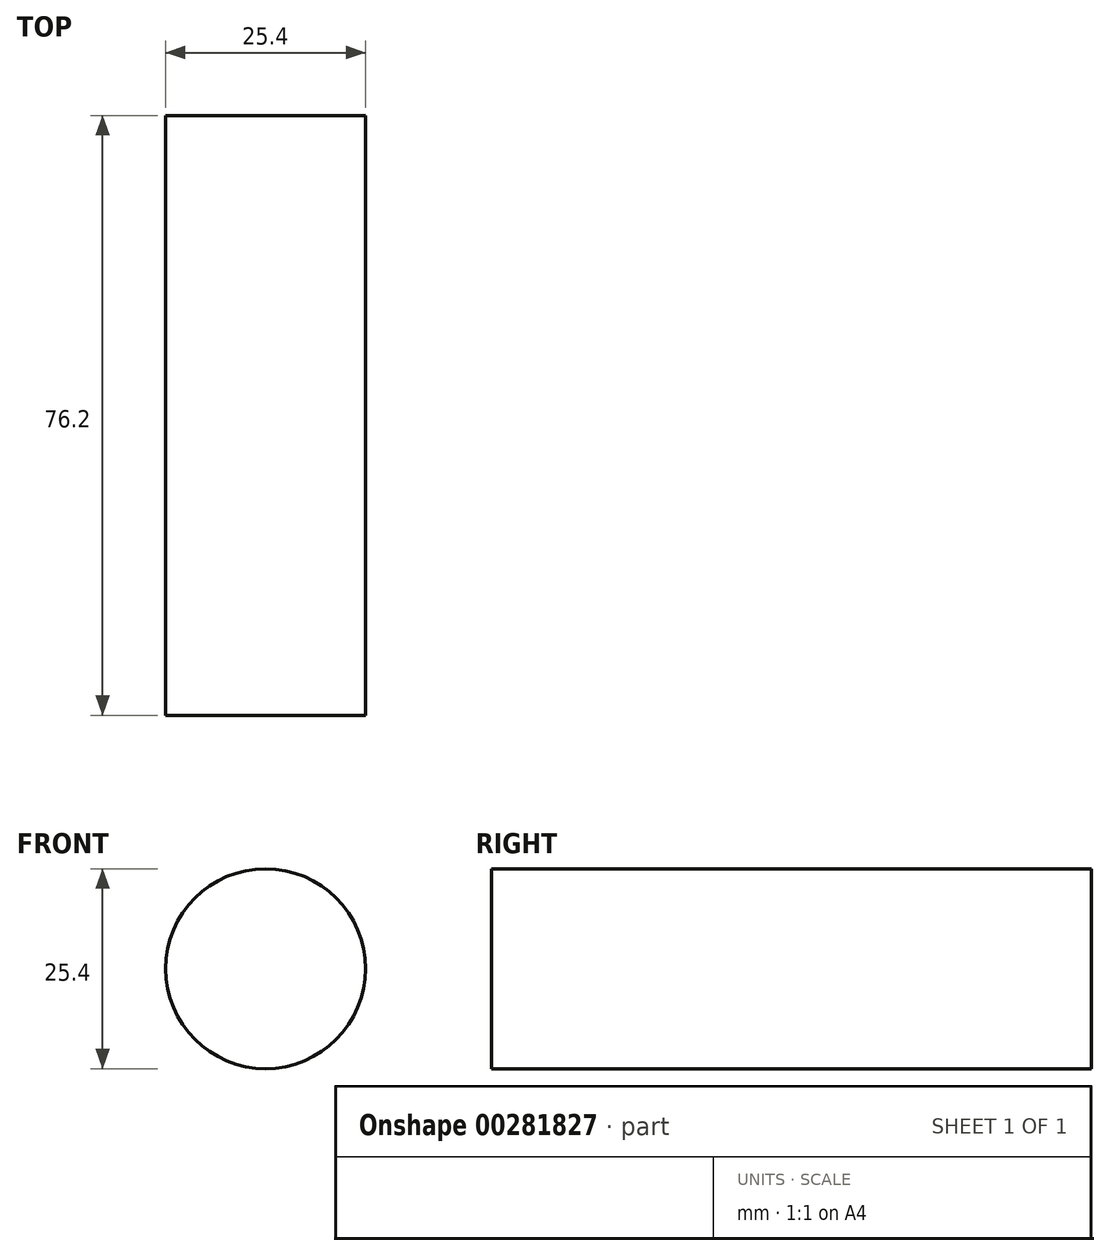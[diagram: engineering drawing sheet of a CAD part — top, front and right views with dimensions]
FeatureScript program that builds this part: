
annotation { "Feature Type Name" : "Feature", "Feature Type Description" : "" }
export const myFeature = defineFeature(function(context is Context, id is Id, definition is map)
    precondition{}
    {
        {
            var Q0;
            Q0=qCreatedBy(makeId("Front.planeOp"),FACE);
            var sketch = newSketch(context, id + "F0", { "sketchPlane" : qUnion([Q0])});
            skCircle(sketch, "E0", {"center": v(0, 0) * mm, "radius": 12.7 * mm});
            skSolve(sketch);
        }
        {
            var Q0;
            Q0=makeQuery(id+"F0.imprint","IMPRINT",FACE,{"disambiguationData":[TD([[makeQuery(id+"F0.imprint","IMPRINT",EDGE,{"derivedFrom":sQuery(id+"F0.wireOp",EDGE,"E0")}),1.0]])]});
            extrude(context, id + "F1", {"entities" : qUnion([Q0]), "depth" : 76.2 * mm});
        }
    });
